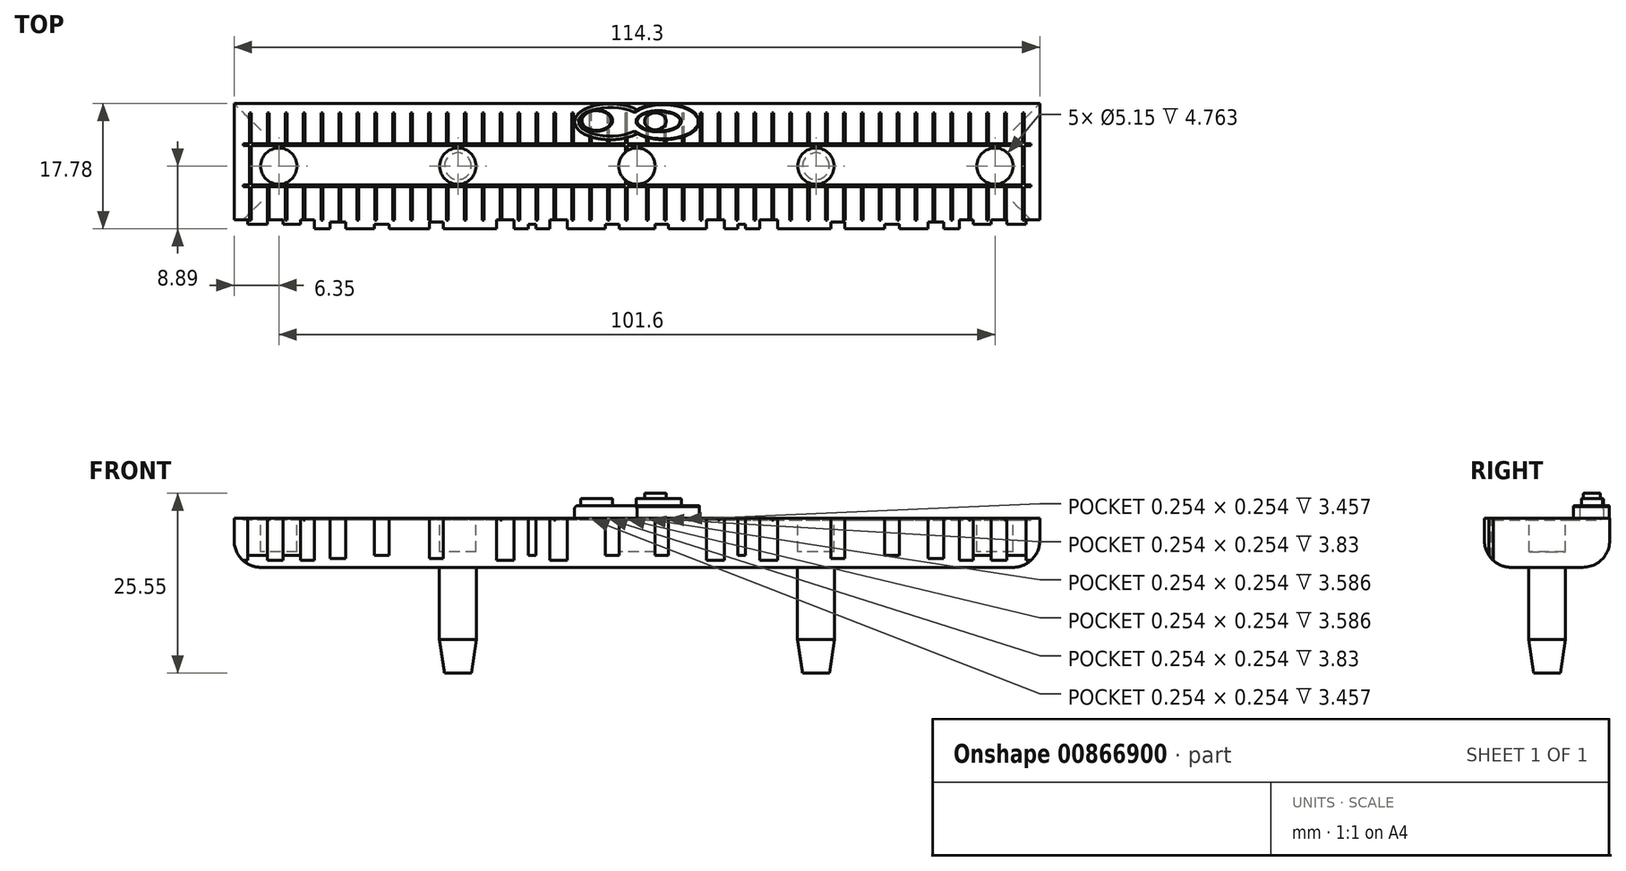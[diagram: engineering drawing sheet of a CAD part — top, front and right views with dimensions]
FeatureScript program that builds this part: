
annotation { "Feature Type Name" : "Feature", "Feature Type Description" : "" }
export const myFeature = defineFeature(function(context is Context, id is Id, definition is map)
    precondition{}
    {
        {
            var Q0;
            Q0=qCreatedBy(makeId("Top.planeOp"),FACE);
            var sketch = newSketch(context, id + "F0", { "sketchPlane" : qUnion([Q0])});
            skLineSegment(sketch, "E0.bottom", {"start": v(57.15, 8.9) * mm, "end": v(-57.15, 8.9) * mm});
            skLineSegment(sketch, "E0.top", {"start": v(57.15, -8.9) * mm, "end": v(-57.15, -8.9) * mm});
            skLineSegment(sketch, "E0.left", {"start": v(57.15, 8.9) * mm, "end": v(57.15, -8.9) * mm});
            skLineSegment(sketch, "E0.right", {"start": v(-57.15, 8.9) * mm, "end": v(-57.15, -8.9) * mm});
            skPoint(sketch, "E0.middle", {"position": v(0, 0) * mm});
            skSolve(sketch);
        }
        {
            var Q0;
            Q0=makeQuery(id+"F0.imprint","IMPRINT",FACE,{"disambiguationData":[TD([[makeQuery(id+"F0.imprint","IMPRINT",EDGE,{"derivedFrom":sQuery(id+"F0.wireOp",EDGE,"E0.bottom")}),1.0]])]});
            extrude(context, id + "F1", {"entities" : qUnion([Q0]), "oppositeDirection" : true, "depth" : 7 * mm, "offsetDistance" : 25.4 * mm});
        }
        {
            var Q0;
            Q0=qCreatedBy(makeId("Top.planeOp"),FACE);
            var sketch = newSketch(context, id + "F2", { "sketchPlane" : qUnion([Q0])});
            skLineSegment(sketch, "E1", {"start": v(0, 0) * mm, "end": v(25.4, 0) * mm, "construction": true});
            skLineSegment(sketch, "E2", {"start": v(25.4, 0) * mm, "end": v(50.8, 0) * mm, "construction": true});
            skLineSegment(sketch, "E3", {"start": v(0, 0) * mm, "end": v(-25.4, 0) * mm, "construction": true});
            skLineSegment(sketch, "E4", {"start": v(-25.4, 0) * mm, "end": v(-50.8, 0) * mm, "construction": true});
            skCircle(sketch, "E5", {"center": v(-50.8, 0) * mm, "radius": 2.58 * mm});
            skCircle(sketch, "E6", {"center": v(-25.4, 0) * mm, "radius": 2.58 * mm});
            skCircle(sketch, "E7", {"center": v(0, 0) * mm, "radius": 2.58 * mm});
            skCircle(sketch, "E8", {"center": v(25.4, 0) * mm, "radius": 2.58 * mm});
            skCircle(sketch, "E9", {"center": v(50.8, 0) * mm, "radius": 2.58 * mm});
            skSolve(sketch);
        }
        {
            var Q0;
            Q0=makeQuery(id+"F1.opExtrude","CAP_FACE",FACE,{"disambiguationData":[OSD([sQuery(id+"F0.wireOp",EDGE,"E0.bottom"),sQuery(id+"F0.wireOp",EDGE,"E0.top"),sQuery(id+"F0.wireOp",EDGE,"E0.left"),sQuery(id+"F0.wireOp",EDGE,"E0.right")])],"isStart":false});
            var sketch = newSketch(context, id + "F3", { "sketchPlane" : qUnion([Q0])});
            skLineSegment(sketch, "E10", {"start": v(0, 0) * mm, "end": v(25.4, 0) * mm, "construction": true});
            skLineSegment(sketch, "E11", {"start": v(25.4, 0) * mm, "end": v(50.8, 0) * mm, "construction": true});
            skLineSegment(sketch, "E12", {"start": v(0, 0) * mm, "end": v(-25.4, 0) * mm, "construction": true});
            skLineSegment(sketch, "E13", {"start": v(-25.4, 0) * mm, "end": v(-50.8, 0) * mm, "construction": true});
            skCircle(sketch, "E14", {"center": v(-50.8, 0) * mm, "radius": 2.62 * mm});
            skCircle(sketch, "E15", {"center": v(-25.4, 0) * mm, "radius": 2.62 * mm});
            skCircle(sketch, "E16", {"center": v(0, 0) * mm, "radius": 2.62 * mm});
            skCircle(sketch, "E17", {"center": v(25.4, 0) * mm, "radius": 2.62 * mm});
            skCircle(sketch, "E18", {"center": v(50.8, 0) * mm, "radius": 2.62 * mm});
            skSolve(sketch);
        }
        {
            var Q0;
            Q0=makeQuery(id+"F2.imprint","IMPRINT",FACE,{"disambiguationData":[TD([[makeQuery(id+"F2.imprint","IMPRINT",EDGE,{"derivedFrom":sQuery(id+"F2.wireOp",EDGE,"E5")}),1.0]])]});
            var Q1;
            Q1=makeQuery(id+"F2.imprint","IMPRINT",FACE,{"disambiguationData":[TD([[makeQuery(id+"F2.imprint","IMPRINT",EDGE,{"derivedFrom":sQuery(id+"F2.wireOp",EDGE,"E6")}),1.0]])]});
            var Q2;
            Q2=makeQuery(id+"F2.imprint","IMPRINT",FACE,{"disambiguationData":[TD([[makeQuery(id+"F2.imprint","IMPRINT",EDGE,{"derivedFrom":sQuery(id+"F2.wireOp",EDGE,"E7")}),1.0]])]});
            var Q3;
            Q3=makeQuery(id+"F2.imprint","IMPRINT",FACE,{"disambiguationData":[TD([[makeQuery(id+"F2.imprint","IMPRINT",EDGE,{"derivedFrom":sQuery(id+"F2.wireOp",EDGE,"E8")}),1.0]])]});
            var Q4;
            Q4=makeQuery(id+"F2.imprint","IMPRINT",FACE,{"disambiguationData":[TD([[makeQuery(id+"F2.imprint","IMPRINT",EDGE,{"derivedFrom":sQuery(id+"F2.wireOp",EDGE,"E9")}),1.0]])]});
            extrude(context, id + "F4", {"entities" : qUnion([Q0, Q1, Q2, Q3, Q4]), "operationType" : NewBodyOperationType.REMOVE, "oppositeDirection" : true, "depth" : 4.76 * mm, "offsetDistance" : 25.4 * mm});
        }
        {
            var Q0;
            Q0=makeQuery(id+"F3.imprint","IMPRINT",FACE,{"disambiguationData":[TD([[makeQuery(id+"F3.imprint","IMPRINT",EDGE,{"derivedFrom":sQuery(id+"F3.wireOp",EDGE,"E15")}),1.0]])]});
            var Q1;
            Q1=makeQuery(id+"F3.imprint","IMPRINT",FACE,{"disambiguationData":[TD([[makeQuery(id+"F3.imprint","IMPRINT",EDGE,{"derivedFrom":sQuery(id+"F3.wireOp",EDGE,"E17")}),1.0]])]});
            extrude(context, id + "F5", {"entities" : qUnion([Q0, Q1]), "operationType" : NewBodyOperationType.ADD, "depth" : 15 * mm, "offsetDistance" : 25.4 * mm});
        }
        {
            var Q0;
            Q0=makeQuery(id+"F5.opExtrude","CAP_EDGE",EDGE,{"disambiguationData":[OSD([sQuery(id+"F3.wireOp",EDGE,"E15")])],"isStart":false});
            var Q1;
            Q1=makeQuery(id+"F5.opExtrude","CAP_EDGE",EDGE,{"disambiguationData":[OSD([sQuery(id+"F3.wireOp",EDGE,"E17")])],"isStart":false});
            chamfer(context, id + "F6", {"entities" : qUnion([Q0, Q1]), "chamferType" : ChamferType.TWO_OFFSETS, "width1" : 0.73 * mm, "oppositeDirection" : false, "width2" : 4.76 * mm, "tangentPropagation" : true});
        }
        {
            var Q0;
            Q0=makeQuery(id+"F1.opExtrude","CAP_EDGE",EDGE,{"disambiguationData":[OSD([sQuery(id+"F0.wireOp",EDGE,"E0.top")])],"isStart":false});
            var Q1;
            Q1=makeQuery(id+"F1.opExtrude","CAP_EDGE",EDGE,{"disambiguationData":[OSD([sQuery(id+"F0.wireOp",EDGE,"E0.left")])],"isStart":false});
            var Q2;
            Q2=makeQuery(id+"F1.opExtrude","CAP_EDGE",EDGE,{"disambiguationData":[OSD([sQuery(id+"F0.wireOp",EDGE,"E0.bottom")])],"isStart":false});
            var Q3;
            Q3=makeQuery(id+"F1.opExtrude","CAP_EDGE",EDGE,{"disambiguationData":[OSD([sQuery(id+"F0.wireOp",EDGE,"E0.right")])],"isStart":false});
            fillet(context, id + "F7", {"entities" : qUnion([Q0, Q1, Q2, Q3]), "radius" : 3.8 * mm, "tangentPropagation" : true, "allowEdgeOverflow" : false});
        }
        {
            var Q0;
            Q0=makeQuery(id+"F1.opExtrude","CAP_FACE",FACE,{"disambiguationData":[OSD([sQuery(id+"F0.wireOp",EDGE,"E0.bottom"),sQuery(id+"F0.wireOp",EDGE,"E0.top"),sQuery(id+"F0.wireOp",EDGE,"E0.left"),sQuery(id+"F0.wireOp",EDGE,"E0.right")])],"isStart":true});
            var sketch = newSketch(context, id + "F8", { "sketchPlane" : qUnion([Q0])});
            skLineSegment(sketch, "E19.bottom", {"start": v(57.15, -8.9) * mm, "end": v(55.22, -8.9) * mm});
            skLineSegment(sketch, "E19.top", {"start": v(57.15, -7.63) * mm, "end": v(55.22, -7.63) * mm});
            skLineSegment(sketch, "E19.left", {"start": v(57.15, -8.9) * mm, "end": v(57.15, -7.63) * mm});
            skLineSegment(sketch, "E19.right", {"start": v(55.22, -8.26) * mm, "end": v(55.22, -7.63) * mm});
            skPoint(sketch, "E20.oppositeSnap0", {"position": v(55.22, -8.26) * mm});
            skLineSegment(sketch, "E20.bottom", {"start": v(55.22, -8.9) * mm, "end": v(52.44, -8.9) * mm});
            skLineSegment(sketch, "E20.top", {"start": v(55.22, -8.26) * mm, "end": v(52.44, -8.26) * mm});
            skLineSegment(sketch, "E21.bottom", {"start": v(52.44, -8.9) * mm, "end": v(50.22, -8.9) * mm});
            skLineSegment(sketch, "E21.top", {"start": v(52.44, -7.63) * mm, "end": v(50.22, -7.63) * mm});
            skLineSegment(sketch, "E21.left", {"start": v(52.44, -8.26) * mm, "end": v(52.44, -7.63) * mm});
            skLineSegment(sketch, "E21.right", {"start": v(50.22, -8.26) * mm, "end": v(50.22, -7.63) * mm});
            skLineSegment(sketch, "E22.bottom", {"start": v(50.22, -8.9) * mm, "end": v(47.71, -8.9) * mm});
            skLineSegment(sketch, "E22.top", {"start": v(50.22, -8.26) * mm, "end": v(47.71, -8.26) * mm});
            skLineSegment(sketch, "E23.bottom", {"start": v(47.71, -8.9) * mm, "end": v(45.77, -8.9) * mm});
            skLineSegment(sketch, "E23.top", {"start": v(47.71, -7.63) * mm, "end": v(45.77, -7.63) * mm});
            skLineSegment(sketch, "E23.left", {"start": v(47.71, -8.26) * mm, "end": v(47.71, -7.63) * mm});
            skLineSegment(sketch, "E23.right", {"start": v(45.77, -8.9) * mm, "end": v(45.77, -7.63) * mm});
            skLineSegment(sketch, "E24.bottom", {"start": v(43.54, -8.9) * mm, "end": v(41.32, -8.9) * mm});
            skLineSegment(sketch, "E24.top", {"start": v(43.54, -7.91) * mm, "end": v(41.32, -7.91) * mm});
            skLineSegment(sketch, "E24.left", {"start": v(43.54, -8.9) * mm, "end": v(43.54, -7.91) * mm});
            skLineSegment(sketch, "E24.right", {"start": v(41.32, -8.9) * mm, "end": v(41.32, -7.91) * mm});
            skLineSegment(sketch, "E25.bottom", {"start": v(35.14, -8.9) * mm, "end": v(37.24, -8.9) * mm});
            skLineSegment(sketch, "E25.top", {"start": v(35.14, -8.26) * mm, "end": v(37.24, -8.26) * mm});
            skLineSegment(sketch, "E25.left", {"start": v(35.14, -8.9) * mm, "end": v(35.14, -8.26) * mm});
            skLineSegment(sketch, "E25.right", {"start": v(37.24, -8.9) * mm, "end": v(37.24, -8.26) * mm});
            skLineSegment(sketch, "E26.bottom", {"start": v(29.46, -8.9) * mm, "end": v(27.49, -8.9) * mm});
            skLineSegment(sketch, "E26.top", {"start": v(29.46, -7.91) * mm, "end": v(27.49, -7.91) * mm});
            skLineSegment(sketch, "E26.left", {"start": v(29.46, -8.9) * mm, "end": v(29.46, -7.91) * mm});
            skLineSegment(sketch, "E26.right", {"start": v(27.49, -8.9) * mm, "end": v(27.49, -7.91) * mm});
            skLineSegment(sketch, "E27.bottom", {"start": v(19.95, -8.9) * mm, "end": v(17.43, -8.9) * mm});
            skLineSegment(sketch, "E27.top", {"start": v(19.95, -7.63) * mm, "end": v(17.43, -7.63) * mm});
            skLineSegment(sketch, "E27.left", {"start": v(19.95, -8.9) * mm, "end": v(19.95, -7.63) * mm});
            skLineSegment(sketch, "E27.right", {"start": v(17.43, -8.9) * mm, "end": v(17.43, -7.63) * mm});
            skPoint(sketch, "E28.oppositeSnap0", {"position": v(18.69, -7.63) * mm});
            skLineSegment(sketch, "E28.bottom", {"start": v(12.38, -8.9) * mm, "end": v(9.86, -8.9) * mm});
            skLineSegment(sketch, "E28.top", {"start": v(12.38, -7.63) * mm, "end": v(9.86, -7.63) * mm});
            skLineSegment(sketch, "E28.left", {"start": v(12.38, -8.9) * mm, "end": v(12.38, -7.63) * mm});
            skLineSegment(sketch, "E28.right", {"start": v(9.86, -8.9) * mm, "end": v(9.86, -7.63) * mm});
            skLineSegment(sketch, "E29.bottom", {"start": v(14.33, -8.9) * mm, "end": v(15.42, -8.9) * mm});
            skLineSegment(sketch, "E29.top", {"start": v(14.33, -8.26) * mm, "end": v(15.42, -8.26) * mm});
            skLineSegment(sketch, "E29.left", {"start": v(14.33, -8.9) * mm, "end": v(14.33, -8.26) * mm});
            skLineSegment(sketch, "E29.right", {"start": v(15.42, -8.9) * mm, "end": v(15.42, -8.26) * mm});
            skLineSegment(sketch, "E30.bottom", {"start": v(2.53, -8.9) * mm, "end": v(4.48, -8.9) * mm});
            skLineSegment(sketch, "E30.top", {"start": v(2.53, -8.26) * mm, "end": v(4.48, -8.26) * mm});
            skLineSegment(sketch, "E30.left", {"start": v(2.53, -8.9) * mm, "end": v(2.53, -8.26) * mm});
            skLineSegment(sketch, "E30.right", {"start": v(4.48, -8.9) * mm, "end": v(4.48, -8.26) * mm});
            skLineSegment(sketch, "E31", {"start": v(0, 15.07) * mm, "end": v(0, 19.04) * mm, "construction": true});
            skLineSegment(sketch, "E32.MirrorCS", {"start": v(-50.22, -8.26) * mm, "end": v(-50.22, -7.63) * mm});
            skLineSegment(sketch, "E33.MirrorCS", {"start": v(-52.44, -8.26) * mm, "end": v(-52.44, -7.63) * mm});
            skLineSegment(sketch, "E34.MirrorCS", {"start": v(-52.44, -7.63) * mm, "end": v(-50.22, -7.63) * mm});
            skLineSegment(sketch, "E35.MirrorCS", {"start": v(-52.44, -8.9) * mm, "end": v(-50.22, -8.9) * mm});
            skLineSegment(sketch, "E36.MirrorCS", {"start": v(-57.15, -7.63) * mm, "end": v(-55.22, -7.63) * mm});
            skLineSegment(sketch, "E37.MirrorCS", {"start": v(-55.22, -8.26) * mm, "end": v(-52.44, -8.26) * mm});
            skLineSegment(sketch, "E38.MirrorCS", {"start": v(-14.33, -8.9) * mm, "end": v(-14.33, -8.26) * mm});
            skLineSegment(sketch, "E39.MirrorCS", {"start": v(-55.22, -8.9) * mm, "end": v(-52.44, -8.9) * mm});
            skLineSegment(sketch, "E40.MirrorCS", {"start": v(-15.42, -8.9) * mm, "end": v(-15.42, -8.26) * mm});
            skLineSegment(sketch, "E41.MirrorCS", {"start": v(-57.15, -8.9) * mm, "end": v(-55.22, -8.9) * mm});
            skLineSegment(sketch, "E42.MirrorCS", {"start": v(-50.22, -8.26) * mm, "end": v(-47.71, -8.26) * mm});
            skLineSegment(sketch, "E43.MirrorCS", {"start": v(-55.22, -8.26) * mm, "end": v(-55.22, -7.63) * mm});
            skLineSegment(sketch, "E44.MirrorCS", {"start": v(-50.22, -8.9) * mm, "end": v(-47.71, -8.9) * mm});
            skLineSegment(sketch, "E45.MirrorCS", {"start": v(-14.33, -8.26) * mm, "end": v(-15.42, -8.26) * mm});
            skLineSegment(sketch, "E46.MirrorCS", {"start": v(-2.53, -8.9) * mm, "end": v(-2.53, -8.26) * mm});
            skLineSegment(sketch, "E47.MirrorCS", {"start": v(-47.71, -7.63) * mm, "end": v(-45.77, -7.63) * mm});
            skLineSegment(sketch, "E48.MirrorCS", {"start": v(-35.14, -8.9) * mm, "end": v(-35.14, -8.26) * mm});
            skLineSegment(sketch, "E49.MirrorCS", {"start": v(-47.71, -8.26) * mm, "end": v(-47.71, -7.63) * mm});
            skLineSegment(sketch, "E50.MirrorCS", {"start": v(-37.24, -8.9) * mm, "end": v(-37.24, -8.26) * mm});
            skLineSegment(sketch, "E51.MirrorCS", {"start": v(-12.38, -8.9) * mm, "end": v(-12.38, -7.63) * mm});
            skLineSegment(sketch, "E52.MirrorCS", {"start": v(-17.43, -8.9) * mm, "end": v(-17.43, -7.63) * mm});
            skLineSegment(sketch, "E53.MirrorCS", {"start": v(-47.71, -8.9) * mm, "end": v(-45.77, -8.9) * mm});
            skLineSegment(sketch, "E54.MirrorCS", {"start": v(-14.33, -8.9) * mm, "end": v(-15.42, -8.9) * mm});
            skLineSegment(sketch, "E55.MirrorCS", {"start": v(-4.48, -8.9) * mm, "end": v(-4.48, -8.26) * mm});
            skLineSegment(sketch, "E56.MirrorCS", {"start": v(-35.14, -8.9) * mm, "end": v(-37.24, -8.9) * mm});
            skLineSegment(sketch, "E57.MirrorCS", {"start": v(-2.53, -8.9) * mm, "end": v(-4.48, -8.9) * mm});
            skLineSegment(sketch, "E58.MirrorCS", {"start": v(-2.53, -8.26) * mm, "end": v(-4.48, -8.26) * mm});
            skLineSegment(sketch, "E59.MirrorCS", {"start": v(-35.14, -8.26) * mm, "end": v(-37.24, -8.26) * mm});
            skLineSegment(sketch, "E60.MirrorCS", {"start": v(-19.95, -8.9) * mm, "end": v(-17.43, -8.9) * mm});
            skLineSegment(sketch, "E61.MirrorCS", {"start": v(-19.95, -7.63) * mm, "end": v(-17.43, -7.63) * mm});
            skLineSegment(sketch, "E62.MirrorCS", {"start": v(-12.38, -7.63) * mm, "end": v(-9.86, -7.63) * mm});
            skLineSegment(sketch, "E63.MirrorCS", {"start": v(-41.32, -8.9) * mm, "end": v(-41.32, -7.91) * mm});
            skLineSegment(sketch, "E64.MirrorCS", {"start": v(-45.77, -8.9) * mm, "end": v(-45.77, -7.63) * mm});
            skLineSegment(sketch, "E65.MirrorCS", {"start": v(-43.54, -8.9) * mm, "end": v(-43.54, -7.91) * mm});
            skLineSegment(sketch, "E66.MirrorCS", {"start": v(-43.54, -8.9) * mm, "end": v(-41.32, -8.9) * mm});
            skLineSegment(sketch, "E67.MirrorCS", {"start": v(-19.95, -8.9) * mm, "end": v(-19.95, -7.63) * mm});
            skLineSegment(sketch, "E68.MirrorCS", {"start": v(-43.54, -7.91) * mm, "end": v(-41.32, -7.91) * mm});
            skLineSegment(sketch, "E69.MirrorCS", {"start": v(-29.46, -8.9) * mm, "end": v(-29.46, -7.91) * mm});
            skLineSegment(sketch, "E70.MirrorCS", {"start": v(-29.46, -7.91) * mm, "end": v(-27.49, -7.91) * mm});
            skLineSegment(sketch, "E71.MirrorCS", {"start": v(-29.46, -8.9) * mm, "end": v(-27.49, -8.9) * mm});
            skLineSegment(sketch, "E72.MirrorCS", {"start": v(-27.49, -8.9) * mm, "end": v(-27.49, -7.91) * mm});
            skLineSegment(sketch, "E73.MirrorCS", {"start": v(-9.86, -8.9) * mm, "end": v(-9.86, -7.63) * mm});
            skLineSegment(sketch, "E74.MirrorCS", {"start": v(-57.15, -8.9) * mm, "end": v(-57.15, -7.63) * mm});
            skLineSegment(sketch, "E75.MirrorCS", {"start": v(-12.38, -8.9) * mm, "end": v(-9.86, -8.9) * mm});
            skPoint(sketch, "E76.MirrorP", {"position": v(-55.22, -8.26) * mm});
            skPoint(sketch, "E77.MirrorP", {"position": v(-18.69, -7.63) * mm});
            skSolve(sketch);
        }
        {
            var Q0;
            Q0=makeQuery(id+"F8.imprint","IMPRINT",FACE,{"disambiguationData":[TD([[makeQuery(id+"F8.imprint","IMPRINT",EDGE,{"derivedFrom":sQuery(id+"F8.wireOp",EDGE,"E30.bottom")}),-1.0]])]});
            var Q1;
            Q1=makeQuery(id+"F8.imprint","IMPRINT",FACE,{"disambiguationData":[TD([[makeQuery(id+"F8.imprint","IMPRINT",EDGE,{"derivedFrom":sQuery(id+"F8.wireOp",EDGE,"E28.bottom")}),-1.0]])]});
            var Q2;
            Q2=makeQuery(id+"F8.imprint","IMPRINT",FACE,{"disambiguationData":[TD([[makeQuery(id+"F8.imprint","IMPRINT",EDGE,{"derivedFrom":sQuery(id+"F8.wireOp",EDGE,"E29.bottom")}),-1.0]])]});
            var Q3;
            Q3=makeQuery(id+"F8.imprint","IMPRINT",FACE,{"disambiguationData":[TD([[makeQuery(id+"F8.imprint","IMPRINT",EDGE,{"derivedFrom":sQuery(id+"F8.wireOp",EDGE,"E27.bottom")}),-1.0]])]});
            var Q4;
            Q4=makeQuery(id+"F8.imprint","IMPRINT",FACE,{"disambiguationData":[TD([[makeQuery(id+"F8.imprint","IMPRINT",EDGE,{"derivedFrom":sQuery(id+"F8.wireOp",EDGE,"E26.bottom")}),-1.0]])]});
            var Q5;
            Q5=makeQuery(id+"F8.imprint","IMPRINT",FACE,{"disambiguationData":[TD([[makeQuery(id+"F8.imprint","IMPRINT",EDGE,{"derivedFrom":sQuery(id+"F8.wireOp",EDGE,"E25.bottom")}),-1.0]])]});
            var Q6;
            Q6=makeQuery(id+"F8.imprint","IMPRINT",FACE,{"disambiguationData":[TD([[makeQuery(id+"F8.imprint","IMPRINT",EDGE,{"derivedFrom":sQuery(id+"F8.wireOp",EDGE,"E24.bottom")}),-1.0]])]});
            var Q7;
            Q7=makeQuery(id+"F8.imprint","IMPRINT",FACE,{"disambiguationData":[TD([[makeQuery(id+"F8.imprint","IMPRINT",EDGE,{"derivedFrom":sQuery(id+"F8.wireOp",EDGE,"E19.bottom")}),-1.0]])]});
            var Q8;
            Q8=makeQuery(id+"F8.imprint","IMPRINT",FACE,{"disambiguationData":[TD([[makeQuery(id+"F8.imprint","IMPRINT",EDGE,{"derivedFrom":sQuery(id+"F8.wireOp",EDGE,"E46.MirrorCS")}),1.0]])]});
            var Q9;
            Q9=makeQuery(id+"F8.imprint","IMPRINT",FACE,{"disambiguationData":[TD([[makeQuery(id+"F8.imprint","IMPRINT",EDGE,{"derivedFrom":sQuery(id+"F8.wireOp",EDGE,"E51.MirrorCS")}),-1.0]])]});
            var Q10;
            Q10=makeQuery(id+"F8.imprint","IMPRINT",FACE,{"disambiguationData":[TD([[makeQuery(id+"F8.imprint","IMPRINT",EDGE,{"derivedFrom":sQuery(id+"F8.wireOp",EDGE,"E38.MirrorCS")}),1.0]])]});
            var Q11;
            Q11=makeQuery(id+"F8.imprint","IMPRINT",FACE,{"disambiguationData":[TD([[makeQuery(id+"F8.imprint","IMPRINT",EDGE,{"derivedFrom":sQuery(id+"F8.wireOp",EDGE,"E52.MirrorCS")}),1.0]])]});
            var Q12;
            Q12=makeQuery(id+"F8.imprint","IMPRINT",FACE,{"disambiguationData":[TD([[makeQuery(id+"F8.imprint","IMPRINT",EDGE,{"derivedFrom":sQuery(id+"F8.wireOp",EDGE,"E69.MirrorCS")}),-1.0]])]});
            var Q13;
            Q13=makeQuery(id+"F8.imprint","IMPRINT",FACE,{"disambiguationData":[TD([[makeQuery(id+"F8.imprint","IMPRINT",EDGE,{"derivedFrom":sQuery(id+"F8.wireOp",EDGE,"E48.MirrorCS")}),1.0]])]});
            var Q14;
            Q14=makeQuery(id+"F8.imprint","IMPRINT",FACE,{"disambiguationData":[TD([[makeQuery(id+"F8.imprint","IMPRINT",EDGE,{"derivedFrom":sQuery(id+"F8.wireOp",EDGE,"E63.MirrorCS")}),1.0]])]});
            var Q15;
            Q15=makeQuery(id+"F8.imprint","IMPRINT",FACE,{"disambiguationData":[TD([[makeQuery(id+"F8.imprint","IMPRINT",EDGE,{"derivedFrom":sQuery(id+"F8.wireOp",EDGE,"E32.MirrorCS")}),1.0]])]});
            extrude(context, id + "F9", {"entities" : qUnion([Q0, Q1, Q2, Q3, Q4, Q5, Q6, Q7, Q8, Q9, Q10, Q11, Q12, Q13, Q14, Q15]), "operationType" : NewBodyOperationType.REMOVE, "endBound" : BoundingType.THROUGH_ALL, "oppositeDirection" : true, "depth" : 25.4 * mm, "offsetDistance" : 25.4 * mm});
        }
        {
            var Q0;
            Q0=makeQuery(id+"F1.opExtrude","CAP_FACE",FACE,{"disambiguationData":[OSD([sQuery(id+"F0.wireOp",EDGE,"E0.bottom"),sQuery(id+"F0.wireOp",EDGE,"E0.top"),sQuery(id+"F0.wireOp",EDGE,"E0.left"),sQuery(id+"F0.wireOp",EDGE,"E0.right")])],"isStart":true});
            var sketch = newSketch(context, id + "F10", { "sketchPlane" : qUnion([Q0])});
            skLineSegment(sketch, "E78", {"start": v(0, 4.02) * mm, "end": v(0, 5.57) * mm, "construction": true});
            skLineSegment(sketch, "E79", {"start": v(0, 2.94) * mm, "end": v(55.88, 2.94) * mm});
            skLineSegment(sketch, "E80", {"start": v(0, -2.68) * mm, "end": v(55.88, -2.68) * mm});
            skLineSegment(sketch, "E81.top", {"start": v(0, 3.2) * mm, "end": v(55.88, 3.2) * mm});
            skLineSegment(sketch, "E81.left", {"start": v(0, 2.94) * mm, "end": v(0, 3.2) * mm});
            skLineSegment(sketch, "E81.right", {"start": v(55.88, 2.94) * mm, "end": v(55.88, 3.2) * mm});
            skLineSegment(sketch, "E82.top", {"start": v(0, -2.93) * mm, "end": v(55.88, -2.93) * mm});
            skLineSegment(sketch, "E82.left", {"start": v(0, -2.68) * mm, "end": v(0, -2.93) * mm});
            skLineSegment(sketch, "E82.right", {"start": v(55.88, -2.68) * mm, "end": v(55.88, -2.93) * mm});
            skLineSegment(sketch, "E83.bottom", {"start": v(1.36, -7.65) * mm, "end": v(1.61, -7.65) * mm});
            skLineSegment(sketch, "E83.top", {"start": v(1.36, 7.59) * mm, "end": v(1.61, 7.59) * mm});
            skLineSegment(sketch, "E83.left", {"start": v(1.36, -7.65) * mm, "end": v(1.36, 7.59) * mm});
            skLineSegment(sketch, "E83.right", {"start": v(1.61, -7.65) * mm, "end": v(1.61, 7.59) * mm});
            skLineSegment(sketch, "E84.MirrorCS", {"start": v(-55.88, -2.68) * mm, "end": v(-55.88, -2.93) * mm});
            skLineSegment(sketch, "E85.MirrorCS", {"start": v(-55.88, 2.94) * mm, "end": v(-55.88, 3.2) * mm});
            skLineSegment(sketch, "E86.MirrorCS", {"start": v(-1.36, -7.65) * mm, "end": v(-1.61, -7.65) * mm});
            skLineSegment(sketch, "E87.MirrorCS", {"start": v(0, -2.68) * mm, "end": v(-55.88, -2.68) * mm});
            skLineSegment(sketch, "E88.MirrorCS", {"start": v(-1.36, 7.59) * mm, "end": v(-1.61, 7.59) * mm});
            skLineSegment(sketch, "E89.MirrorCS", {"start": v(0, 2.94) * mm, "end": v(-55.88, 2.94) * mm});
            skLineSegment(sketch, "E90.MirrorCS", {"start": v(0, -2.93) * mm, "end": v(-55.88, -2.93) * mm});
            skLineSegment(sketch, "E91.MirrorCS", {"start": v(-1.61, -7.65) * mm, "end": v(-1.61, 7.59) * mm});
            skLineSegment(sketch, "E92.MirrorCS", {"start": v(-1.36, -7.65) * mm, "end": v(-1.36, 7.59) * mm});
            skLineSegment(sketch, "E93.MirrorCS", {"start": v(0, 3.2) * mm, "end": v(-55.88, 3.2) * mm});
            skLineSegment(sketch, "E94.1.0.0", {"start": v(3.9, -7.65) * mm, "end": v(3.9, 7.59) * mm});
            skLineSegment(sketch, "E94.1.0.1", {"start": v(4.15, -7.65) * mm, "end": v(4.15, 7.59) * mm});
            skLineSegment(sketch, "E94.1.0.2", {"start": v(3.9, 7.59) * mm, "end": v(4.15, 7.59) * mm});
            skLineSegment(sketch, "E94.1.0.3", {"start": v(3.9, -7.65) * mm, "end": v(4.15, -7.65) * mm});
            skLineSegment(sketch, "E94.2.0.0", {"start": v(6.44, -7.65) * mm, "end": v(6.44, 7.59) * mm});
            skLineSegment(sketch, "E94.2.0.1", {"start": v(6.7, -7.65) * mm, "end": v(6.7, 7.59) * mm});
            skLineSegment(sketch, "E94.2.0.2", {"start": v(6.44, 7.59) * mm, "end": v(6.7, 7.59) * mm});
            skLineSegment(sketch, "E94.2.0.3", {"start": v(6.44, -7.65) * mm, "end": v(6.7, -7.65) * mm});
            skLineSegment(sketch, "E94.3.0.0", {"start": v(8.98, -7.65) * mm, "end": v(8.98, 7.59) * mm});
            skLineSegment(sketch, "E94.3.0.1", {"start": v(9.23, -7.65) * mm, "end": v(9.23, 7.59) * mm});
            skLineSegment(sketch, "E94.3.0.2", {"start": v(8.98, 7.59) * mm, "end": v(9.23, 7.59) * mm});
            skLineSegment(sketch, "E94.3.0.3", {"start": v(8.98, -7.65) * mm, "end": v(9.23, -7.65) * mm});
            skLineSegment(sketch, "E94.4.0.0", {"start": v(11.52, -7.65) * mm, "end": v(11.52, 7.59) * mm});
            skLineSegment(sketch, "E94.4.0.1", {"start": v(11.77, -7.65) * mm, "end": v(11.77, 7.59) * mm});
            skLineSegment(sketch, "E94.4.0.2", {"start": v(11.52, 7.59) * mm, "end": v(11.77, 7.59) * mm});
            skLineSegment(sketch, "E94.4.0.3", {"start": v(11.52, -7.65) * mm, "end": v(11.77, -7.65) * mm});
            skLineSegment(sketch, "E94.5.0.0", {"start": v(14.06, -7.65) * mm, "end": v(14.06, 7.59) * mm});
            skLineSegment(sketch, "E94.5.0.1", {"start": v(14.31, -7.65) * mm, "end": v(14.31, 7.59) * mm});
            skLineSegment(sketch, "E94.5.0.2", {"start": v(14.06, 7.59) * mm, "end": v(14.31, 7.59) * mm});
            skLineSegment(sketch, "E94.5.0.3", {"start": v(14.06, -7.65) * mm, "end": v(14.31, -7.65) * mm});
            skLineSegment(sketch, "E94.6.0.0", {"start": v(16.6, -7.65) * mm, "end": v(16.6, 7.59) * mm});
            skLineSegment(sketch, "E94.6.0.1", {"start": v(16.85, -7.65) * mm, "end": v(16.85, 7.59) * mm});
            skLineSegment(sketch, "E94.6.0.2", {"start": v(16.6, 7.59) * mm, "end": v(16.85, 7.59) * mm});
            skLineSegment(sketch, "E94.6.0.3", {"start": v(16.6, -7.65) * mm, "end": v(16.85, -7.65) * mm});
            skLineSegment(sketch, "E94.7.0.0", {"start": v(19.14, -7.65) * mm, "end": v(19.14, 7.59) * mm});
            skLineSegment(sketch, "E94.7.0.1", {"start": v(19.4, -7.65) * mm, "end": v(19.4, 7.59) * mm});
            skLineSegment(sketch, "E94.7.0.2", {"start": v(19.14, 7.59) * mm, "end": v(19.4, 7.59) * mm});
            skLineSegment(sketch, "E94.7.0.3", {"start": v(19.14, -7.65) * mm, "end": v(19.4, -7.65) * mm});
            skLineSegment(sketch, "E94.8.0.0", {"start": v(21.68, -7.65) * mm, "end": v(21.68, 7.59) * mm});
            skLineSegment(sketch, "E94.8.0.1", {"start": v(21.93, -7.65) * mm, "end": v(21.93, 7.59) * mm});
            skLineSegment(sketch, "E94.8.0.2", {"start": v(21.68, 7.59) * mm, "end": v(21.93, 7.59) * mm});
            skLineSegment(sketch, "E94.8.0.3", {"start": v(21.68, -7.65) * mm, "end": v(21.93, -7.65) * mm});
            skLineSegment(sketch, "E94.9.0.0", {"start": v(24.22, -7.65) * mm, "end": v(24.22, 7.59) * mm});
            skLineSegment(sketch, "E94.9.0.1", {"start": v(24.47, -7.65) * mm, "end": v(24.47, 7.59) * mm});
            skLineSegment(sketch, "E94.9.0.2", {"start": v(24.22, 7.59) * mm, "end": v(24.47, 7.59) * mm});
            skLineSegment(sketch, "E94.9.0.3", {"start": v(24.22, -7.65) * mm, "end": v(24.47, -7.65) * mm});
            skLineSegment(sketch, "E94.10.0.0", {"start": v(26.76, -7.65) * mm, "end": v(26.76, 7.59) * mm});
            skLineSegment(sketch, "E94.10.0.1", {"start": v(27.01, -7.65) * mm, "end": v(27.01, 7.59) * mm});
            skLineSegment(sketch, "E94.10.0.2", {"start": v(26.76, 7.59) * mm, "end": v(27.01, 7.59) * mm});
            skLineSegment(sketch, "E94.10.0.3", {"start": v(26.76, -7.65) * mm, "end": v(27.01, -7.65) * mm});
            skLineSegment(sketch, "E94.11.0.0", {"start": v(29.3, -7.65) * mm, "end": v(29.3, 7.59) * mm});
            skLineSegment(sketch, "E94.11.0.1", {"start": v(29.55, -7.65) * mm, "end": v(29.55, 7.59) * mm});
            skLineSegment(sketch, "E94.11.0.2", {"start": v(29.3, 7.59) * mm, "end": v(29.55, 7.59) * mm});
            skLineSegment(sketch, "E94.11.0.3", {"start": v(29.3, -7.65) * mm, "end": v(29.55, -7.65) * mm});
            skLineSegment(sketch, "E94.12.0.0", {"start": v(31.84, -7.65) * mm, "end": v(31.84, 7.59) * mm});
            skLineSegment(sketch, "E94.12.0.1", {"start": v(32.1, -7.65) * mm, "end": v(32.1, 7.59) * mm});
            skLineSegment(sketch, "E94.12.0.2", {"start": v(31.84, 7.59) * mm, "end": v(32.1, 7.59) * mm});
            skLineSegment(sketch, "E94.12.0.3", {"start": v(31.84, -7.65) * mm, "end": v(32.1, -7.65) * mm});
            skLineSegment(sketch, "E94.13.0.0", {"start": v(34.38, -7.65) * mm, "end": v(34.38, 7.59) * mm});
            skLineSegment(sketch, "E94.13.0.1", {"start": v(34.63, -7.65) * mm, "end": v(34.63, 7.59) * mm});
            skLineSegment(sketch, "E94.13.0.2", {"start": v(34.38, 7.59) * mm, "end": v(34.63, 7.59) * mm});
            skLineSegment(sketch, "E94.13.0.3", {"start": v(34.38, -7.65) * mm, "end": v(34.63, -7.65) * mm});
            skLineSegment(sketch, "E94.14.0.0", {"start": v(36.92, -7.65) * mm, "end": v(36.92, 7.59) * mm});
            skLineSegment(sketch, "E94.14.0.1", {"start": v(37.17, -7.65) * mm, "end": v(37.17, 7.59) * mm});
            skLineSegment(sketch, "E94.14.0.2", {"start": v(36.92, 7.59) * mm, "end": v(37.17, 7.59) * mm});
            skLineSegment(sketch, "E94.14.0.3", {"start": v(36.92, -7.65) * mm, "end": v(37.17, -7.65) * mm});
            skLineSegment(sketch, "E94.15.0.0", {"start": v(39.46, -7.65) * mm, "end": v(39.46, 7.59) * mm});
            skLineSegment(sketch, "E94.15.0.1", {"start": v(39.71, -7.65) * mm, "end": v(39.71, 7.59) * mm});
            skLineSegment(sketch, "E94.15.0.2", {"start": v(39.46, 7.59) * mm, "end": v(39.71, 7.59) * mm});
            skLineSegment(sketch, "E94.15.0.3", {"start": v(39.46, -7.65) * mm, "end": v(39.71, -7.65) * mm});
            skLineSegment(sketch, "E94.16.0.0", {"start": v(42, -7.65) * mm, "end": v(42, 7.59) * mm});
            skLineSegment(sketch, "E94.16.0.1", {"start": v(42.25, -7.65) * mm, "end": v(42.25, 7.59) * mm});
            skLineSegment(sketch, "E94.16.0.2", {"start": v(42, 7.59) * mm, "end": v(42.25, 7.59) * mm});
            skLineSegment(sketch, "E94.16.0.3", {"start": v(42, -7.65) * mm, "end": v(42.25, -7.65) * mm});
            skLineSegment(sketch, "E94.17.0.0", {"start": v(44.54, -7.65) * mm, "end": v(44.54, 7.59) * mm});
            skLineSegment(sketch, "E94.17.0.1", {"start": v(44.8, -7.65) * mm, "end": v(44.8, 7.59) * mm});
            skLineSegment(sketch, "E94.17.0.2", {"start": v(44.54, 7.59) * mm, "end": v(44.8, 7.59) * mm});
            skLineSegment(sketch, "E94.17.0.3", {"start": v(44.54, -7.65) * mm, "end": v(44.8, -7.65) * mm});
            skLineSegment(sketch, "E94.18.0.0", {"start": v(47.08, -7.65) * mm, "end": v(47.08, 7.59) * mm});
            skLineSegment(sketch, "E94.18.0.1", {"start": v(47.33, -7.65) * mm, "end": v(47.33, 7.59) * mm});
            skLineSegment(sketch, "E94.18.0.2", {"start": v(47.08, 7.59) * mm, "end": v(47.33, 7.59) * mm});
            skLineSegment(sketch, "E94.18.0.3", {"start": v(47.08, -7.65) * mm, "end": v(47.33, -7.65) * mm});
            skLineSegment(sketch, "E94.19.0.0", {"start": v(49.62, -7.65) * mm, "end": v(49.62, 7.59) * mm});
            skLineSegment(sketch, "E94.19.0.1", {"start": v(49.87, -7.65) * mm, "end": v(49.87, 7.59) * mm});
            skLineSegment(sketch, "E94.19.0.2", {"start": v(49.62, 7.59) * mm, "end": v(49.87, 7.59) * mm});
            skLineSegment(sketch, "E94.19.0.3", {"start": v(49.62, -7.65) * mm, "end": v(49.87, -7.65) * mm});
            skLineSegment(sketch, "E94.20.0.0", {"start": v(52.16, -7.65) * mm, "end": v(52.16, 7.59) * mm});
            skLineSegment(sketch, "E94.20.0.1", {"start": v(52.41, -7.65) * mm, "end": v(52.41, 7.59) * mm});
            skLineSegment(sketch, "E94.20.0.2", {"start": v(52.16, 7.59) * mm, "end": v(52.41, 7.59) * mm});
            skLineSegment(sketch, "E94.20.0.3", {"start": v(52.16, -7.65) * mm, "end": v(52.41, -7.65) * mm});
            skLineSegment(sketch, "E94.21.0.0", {"start": v(54.7, -7.65) * mm, "end": v(54.7, 7.59) * mm});
            skLineSegment(sketch, "E94.21.0.1", {"start": v(54.95, -7.65) * mm, "end": v(54.95, 7.59) * mm});
            skLineSegment(sketch, "E94.21.0.2", {"start": v(54.7, 7.59) * mm, "end": v(54.95, 7.59) * mm});
            skLineSegment(sketch, "E94.21.0.3", {"start": v(54.7, -7.65) * mm, "end": v(54.95, -7.65) * mm});
            skLineSegment(sketch, "E94.direction1", {"start": v(1.36, -7.65) * mm, "end": v(3.9, -7.65) * mm, "construction": true});
            skLineSegment(sketch, "E95.MirrorCS", {"start": v(-3.9, -7.65) * mm, "end": v(-4.15, -7.65) * mm});
            skLineSegment(sketch, "E96.MirrorCS", {"start": v(-26.76, -7.65) * mm, "end": v(-27.01, -7.65) * mm});
            skLineSegment(sketch, "E97.MirrorCS", {"start": v(-42, 7.59) * mm, "end": v(-42.25, 7.59) * mm});
            skLineSegment(sketch, "E98.MirrorCS", {"start": v(-11.52, 7.59) * mm, "end": v(-11.77, 7.59) * mm});
            skLineSegment(sketch, "E99.MirrorCS", {"start": v(-34.38, -7.65) * mm, "end": v(-34.63, -7.65) * mm});
            skLineSegment(sketch, "E100.MirrorCS", {"start": v(-49.62, -7.65) * mm, "end": v(-49.87, -7.65) * mm});
            skLineSegment(sketch, "E101.MirrorCS", {"start": v(-19.14, -7.65) * mm, "end": v(-19.4, -7.65) * mm});
            skLineSegment(sketch, "E102.MirrorCS", {"start": v(-3.9, 7.59) * mm, "end": v(-4.15, 7.59) * mm});
            skLineSegment(sketch, "E103.MirrorCS", {"start": v(-19.14, 7.59) * mm, "end": v(-19.4, 7.59) * mm});
            skLineSegment(sketch, "E104.MirrorCS", {"start": v(-42, -7.65) * mm, "end": v(-42.25, -7.65) * mm});
            skLineSegment(sketch, "E105.MirrorCS", {"start": v(-11.52, -7.65) * mm, "end": v(-11.77, -7.65) * mm});
            skLineSegment(sketch, "E106.MirrorCS", {"start": v(-34.38, 7.59) * mm, "end": v(-34.63, 7.59) * mm});
            skLineSegment(sketch, "E107.MirrorCS", {"start": v(-49.62, 7.59) * mm, "end": v(-49.87, 7.59) * mm});
            skLineSegment(sketch, "E108.MirrorCS", {"start": v(-26.76, 7.59) * mm, "end": v(-27.01, 7.59) * mm});
            skLineSegment(sketch, "E109.MirrorCS", {"start": v(-16.6, -7.65) * mm, "end": v(-16.85, -7.65) * mm});
            skLineSegment(sketch, "E110.MirrorCS", {"start": v(-36.92, -7.65) * mm, "end": v(-37.17, -7.65) * mm});
            skLineSegment(sketch, "E111.MirrorCS", {"start": v(-47.08, -7.65) * mm, "end": v(-47.33, -7.65) * mm});
            skLineSegment(sketch, "E112.MirrorCS", {"start": v(-6.44, -7.65) * mm, "end": v(-6.7, -7.65) * mm});
            skLineSegment(sketch, "E113.MirrorCS", {"start": v(-52.16, 7.59) * mm, "end": v(-52.41, 7.59) * mm});
            skLineSegment(sketch, "E114.MirrorCS", {"start": v(-21.68, 7.59) * mm, "end": v(-21.93, 7.59) * mm});
            skLineSegment(sketch, "E115.MirrorCS", {"start": v(-31.84, 7.59) * mm, "end": v(-32.1, 7.59) * mm});
            skLineSegment(sketch, "E116.MirrorCS", {"start": v(-54.7, -7.65) * mm, "end": v(-54.95, -7.65) * mm});
            skLineSegment(sketch, "E117.MirrorCS", {"start": v(-14.06, -7.65) * mm, "end": v(-14.31, -7.65) * mm});
            skLineSegment(sketch, "E118.MirrorCS", {"start": v(-24.22, -7.65) * mm, "end": v(-24.47, -7.65) * mm});
            skLineSegment(sketch, "E119.MirrorCS", {"start": v(-44.54, -7.65) * mm, "end": v(-44.8, -7.65) * mm});
            skLineSegment(sketch, "E120.MirrorCS", {"start": v(-39.46, -7.65) * mm, "end": v(-39.71, -7.65) * mm});
            skLineSegment(sketch, "E121.MirrorCS", {"start": v(-8.98, -7.65) * mm, "end": v(-9.23, -7.65) * mm});
            skLineSegment(sketch, "E122.MirrorCS", {"start": v(-29.3, -7.65) * mm, "end": v(-29.55, -7.65) * mm});
            skLineSegment(sketch, "E123.MirrorCS", {"start": v(-6.44, 7.59) * mm, "end": v(-6.7, 7.59) * mm});
            skLineSegment(sketch, "E124.MirrorCS", {"start": v(-14.06, 7.59) * mm, "end": v(-14.31, 7.59) * mm});
            skLineSegment(sketch, "E125.MirrorCS", {"start": v(-52.16, -7.65) * mm, "end": v(-52.41, -7.65) * mm});
            skLineSegment(sketch, "E126.MirrorCS", {"start": v(-39.46, 7.59) * mm, "end": v(-39.71, 7.59) * mm});
            skLineSegment(sketch, "E127.MirrorCS", {"start": v(-54.7, 7.59) * mm, "end": v(-54.95, 7.59) * mm});
            skLineSegment(sketch, "E128.MirrorCS", {"start": v(-8.98, 7.59) * mm, "end": v(-9.23, 7.59) * mm});
            skLineSegment(sketch, "E129.MirrorCS", {"start": v(-21.68, -7.65) * mm, "end": v(-21.93, -7.65) * mm});
            skLineSegment(sketch, "E130.MirrorCS", {"start": v(-29.3, 7.59) * mm, "end": v(-29.55, 7.59) * mm});
            skLineSegment(sketch, "E131.MirrorCS", {"start": v(-24.22, 7.59) * mm, "end": v(-24.47, 7.59) * mm});
            skLineSegment(sketch, "E132.MirrorCS", {"start": v(-31.84, -7.65) * mm, "end": v(-32.1, -7.65) * mm});
            skLineSegment(sketch, "E133.MirrorCS", {"start": v(-16.6, 7.59) * mm, "end": v(-16.85, 7.59) * mm});
            skLineSegment(sketch, "E134.MirrorCS", {"start": v(-36.92, 7.59) * mm, "end": v(-37.17, 7.59) * mm});
            skLineSegment(sketch, "E135.MirrorCS", {"start": v(-44.54, 7.59) * mm, "end": v(-44.8, 7.59) * mm});
            skLineSegment(sketch, "E136.MirrorCS", {"start": v(-47.08, 7.59) * mm, "end": v(-47.33, 7.59) * mm});
            skLineSegment(sketch, "E137.MirrorCS", {"start": v(-19.14, -7.65) * mm, "end": v(-19.14, 7.59) * mm});
            skLineSegment(sketch, "E138.MirrorCS", {"start": v(-34.63, -7.65) * mm, "end": v(-34.63, 7.59) * mm});
            skLineSegment(sketch, "E139.MirrorCS", {"start": v(-49.62, -7.65) * mm, "end": v(-49.62, 7.59) * mm});
            skLineSegment(sketch, "E140.MirrorCS", {"start": v(-42, -7.65) * mm, "end": v(-42, 7.59) * mm});
            skLineSegment(sketch, "E141.MirrorCS", {"start": v(-4.15, -7.65) * mm, "end": v(-4.15, 7.59) * mm});
            skLineSegment(sketch, "E142.MirrorCS", {"start": v(-26.76, -7.65) * mm, "end": v(-26.76, 7.59) * mm});
            skLineSegment(sketch, "E143.MirrorCS", {"start": v(-11.52, -7.65) * mm, "end": v(-11.52, 7.59) * mm});
            skLineSegment(sketch, "E144.MirrorCS", {"start": v(-14.06, -7.65) * mm, "end": v(-14.06, 7.59) * mm});
            skLineSegment(sketch, "E145.MirrorCS", {"start": v(-24.22, -7.65) * mm, "end": v(-24.22, 7.59) * mm});
            skLineSegment(sketch, "E146.MirrorCS", {"start": v(-34.38, -7.65) * mm, "end": v(-34.38, 7.59) * mm});
            skLineSegment(sketch, "E147.MirrorCS", {"start": v(-44.54, -7.65) * mm, "end": v(-44.54, 7.59) * mm});
            skLineSegment(sketch, "E148.MirrorCS", {"start": v(-3.9, -7.65) * mm, "end": v(-3.9, 7.59) * mm});
            skLineSegment(sketch, "E149.MirrorCS", {"start": v(-16.85, -7.65) * mm, "end": v(-16.85, 7.59) * mm});
            skLineSegment(sketch, "E150.MirrorCS", {"start": v(-27.01, -7.65) * mm, "end": v(-27.01, 7.59) * mm});
            skLineSegment(sketch, "E151.MirrorCS", {"start": v(-37.17, -7.65) * mm, "end": v(-37.17, 7.59) * mm});
            skLineSegment(sketch, "E152.MirrorCS", {"start": v(-47.33, -7.65) * mm, "end": v(-47.33, 7.59) * mm});
            skLineSegment(sketch, "E153.MirrorCS", {"start": v(-54.7, -7.65) * mm, "end": v(-54.7, 7.59) * mm});
            skLineSegment(sketch, "E154.MirrorCS", {"start": v(-6.7, -7.65) * mm, "end": v(-6.7, 7.59) * mm});
            skLineSegment(sketch, "E155.MirrorCS", {"start": v(-39.71, -7.65) * mm, "end": v(-39.71, 7.59) * mm});
            skLineSegment(sketch, "E156.MirrorCS", {"start": v(-49.87, -7.65) * mm, "end": v(-49.87, 7.59) * mm});
            skLineSegment(sketch, "E157.MirrorCS", {"start": v(-9.23, -7.65) * mm, "end": v(-9.23, 7.59) * mm});
            skLineSegment(sketch, "E158.MirrorCS", {"start": v(-19.4, -7.65) * mm, "end": v(-19.4, 7.59) * mm});
            skLineSegment(sketch, "E159.MirrorCS", {"start": v(-29.55, -7.65) * mm, "end": v(-29.55, 7.59) * mm});
            skLineSegment(sketch, "E160.MirrorCS", {"start": v(-42.25, -7.65) * mm, "end": v(-42.25, 7.59) * mm});
            skLineSegment(sketch, "E161.MirrorCS", {"start": v(-52.41, -7.65) * mm, "end": v(-52.41, 7.59) * mm});
            skLineSegment(sketch, "E162.MirrorCS", {"start": v(-54.95, -7.65) * mm, "end": v(-54.95, 7.59) * mm});
            skLineSegment(sketch, "E163.MirrorCS", {"start": v(-14.31, -7.65) * mm, "end": v(-14.31, 7.59) * mm});
            skLineSegment(sketch, "E164.MirrorCS", {"start": v(-29.3, -7.65) * mm, "end": v(-29.3, 7.59) * mm});
            skLineSegment(sketch, "E165.MirrorCS", {"start": v(-24.47, -7.65) * mm, "end": v(-24.47, 7.59) * mm});
            skLineSegment(sketch, "E166.MirrorCS", {"start": v(-39.46, -7.65) * mm, "end": v(-39.46, 7.59) * mm});
            skLineSegment(sketch, "E167.MirrorCS", {"start": v(-44.8, -7.65) * mm, "end": v(-44.8, 7.59) * mm});
            skLineSegment(sketch, "E168.MirrorCS", {"start": v(-36.92, -7.65) * mm, "end": v(-36.92, 7.59) * mm});
            skLineSegment(sketch, "E169.MirrorCS", {"start": v(-47.08, -7.65) * mm, "end": v(-47.08, 7.59) * mm});
            skLineSegment(sketch, "E170.MirrorCS", {"start": v(-31.84, -7.65) * mm, "end": v(-31.84, 7.59) * mm});
            skLineSegment(sketch, "E171.MirrorCS", {"start": v(-21.68, -7.65) * mm, "end": v(-21.68, 7.59) * mm});
            skLineSegment(sketch, "E172.MirrorCS", {"start": v(-32.1, -7.65) * mm, "end": v(-32.1, 7.59) * mm});
            skLineSegment(sketch, "E173.MirrorCS", {"start": v(-11.77, -7.65) * mm, "end": v(-11.77, 7.59) * mm});
            skLineSegment(sketch, "E174.MirrorCS", {"start": v(-16.6, -7.65) * mm, "end": v(-16.6, 7.59) * mm});
            skLineSegment(sketch, "E175.MirrorCS", {"start": v(-52.16, -7.65) * mm, "end": v(-52.16, 7.59) * mm});
            skLineSegment(sketch, "E176.MirrorCS", {"start": v(-21.93, -7.65) * mm, "end": v(-21.93, 7.59) * mm});
            skLineSegment(sketch, "E177.MirrorCS", {"start": v(-8.98, -7.65) * mm, "end": v(-8.98, 7.59) * mm});
            skLineSegment(sketch, "E178.MirrorCS", {"start": v(-6.44, -7.65) * mm, "end": v(-6.44, 7.59) * mm});
            skSolve(sketch);
        }
        {
            var Q0;
            Q0 = qSketchRegion(id + "F10", true);
            var Q1;
            {var subQ0=sQuery(id+"F10.wireOp",EDGE,"E94.20.0.0");var subQ1=sQuery(id+"F10.wireOp",EDGE,"E80");var subQ2=makeQuery(id+"F10.imprint","INTERSECT",VERTEX,{"derivedFrom":[subQ1,subQ0]});Q1=makeQuery(id+"F10.imprint","IMPRINT",FACE,{"disambiguationData":[TD([[makeQuery(id+"F10.imprint","IMPRINT",EDGE,{"disambiguationData":[TD([[subQ2,-1.0]])],"derivedFrom":subQ1}),1.0]])]});}
            var Q2;
            {var subQ0=sQuery(id+"F10.wireOp",EDGE,"E94.19.0.0");var subQ1=sQuery(id+"F10.wireOp",EDGE,"E79");var subQ2=makeQuery(id+"F10.imprint","INTERSECT",VERTEX,{"derivedFrom":[subQ1,subQ0]});Q2=makeQuery(id+"F10.imprint","IMPRINT",FACE,{"disambiguationData":[TD([[makeQuery(id+"F10.imprint","IMPRINT",EDGE,{"disambiguationData":[TD([[subQ2,-1.0]])],"derivedFrom":subQ1}),-1.0]])]});}
            var Q3;
            {var subQ0=sQuery(id+"F10.wireOp",EDGE,"E94.19.0.0");var subQ1=sQuery(id+"F10.wireOp",EDGE,"E80");var subQ2=makeQuery(id+"F10.imprint","INTERSECT",VERTEX,{"derivedFrom":[subQ1,subQ0]});Q3=makeQuery(id+"F10.imprint","IMPRINT",FACE,{"disambiguationData":[TD([[makeQuery(id+"F10.imprint","IMPRINT",EDGE,{"disambiguationData":[TD([[subQ2,-1.0]])],"derivedFrom":subQ1}),1.0]])]});}
            var Q4;
            {var subQ0=sQuery(id+"F10.wireOp",EDGE,"E94.18.0.0");var subQ1=sQuery(id+"F10.wireOp",EDGE,"E79");var subQ2=makeQuery(id+"F10.imprint","INTERSECT",VERTEX,{"derivedFrom":[subQ1,subQ0]});Q4=makeQuery(id+"F10.imprint","IMPRINT",FACE,{"disambiguationData":[TD([[makeQuery(id+"F10.imprint","IMPRINT",EDGE,{"disambiguationData":[TD([[subQ2,-1.0]])],"derivedFrom":subQ1}),-1.0]])]});}
            var Q5;
            {var subQ0=sQuery(id+"F10.wireOp",EDGE,"E94.17.0.0");var subQ1=sQuery(id+"F10.wireOp",EDGE,"E79");var subQ2=makeQuery(id+"F10.imprint","INTERSECT",VERTEX,{"derivedFrom":[subQ1,subQ0]});Q5=makeQuery(id+"F10.imprint","IMPRINT",FACE,{"disambiguationData":[TD([[makeQuery(id+"F10.imprint","IMPRINT",EDGE,{"disambiguationData":[TD([[subQ2,-1.0]])],"derivedFrom":subQ1}),-1.0]])]});}
            var Q6;
            {var subQ0=sQuery(id+"F10.wireOp",EDGE,"E94.16.0.0");var subQ1=sQuery(id+"F10.wireOp",EDGE,"E79");var subQ2=makeQuery(id+"F10.imprint","INTERSECT",VERTEX,{"derivedFrom":[subQ1,subQ0]});Q6=makeQuery(id+"F10.imprint","IMPRINT",FACE,{"disambiguationData":[TD([[makeQuery(id+"F10.imprint","IMPRINT",EDGE,{"disambiguationData":[TD([[subQ2,-1.0]])],"derivedFrom":subQ1}),-1.0]])]});}
            var Q7;
            {var subQ0=sQuery(id+"F10.wireOp",EDGE,"E94.15.0.0");var subQ1=sQuery(id+"F10.wireOp",EDGE,"E79");var subQ2=makeQuery(id+"F10.imprint","INTERSECT",VERTEX,{"derivedFrom":[subQ1,subQ0]});Q7=makeQuery(id+"F10.imprint","IMPRINT",FACE,{"disambiguationData":[TD([[makeQuery(id+"F10.imprint","IMPRINT",EDGE,{"disambiguationData":[TD([[subQ2,-1.0]])],"derivedFrom":subQ1}),-1.0]])]});}
            var Q8;
            {var subQ0=sQuery(id+"F10.wireOp",EDGE,"E94.14.0.0");var subQ1=sQuery(id+"F10.wireOp",EDGE,"E79");var subQ2=makeQuery(id+"F10.imprint","INTERSECT",VERTEX,{"derivedFrom":[subQ1,subQ0]});Q8=makeQuery(id+"F10.imprint","IMPRINT",FACE,{"disambiguationData":[TD([[makeQuery(id+"F10.imprint","IMPRINT",EDGE,{"disambiguationData":[TD([[subQ2,-1.0]])],"derivedFrom":subQ1}),-1.0]])]});}
            var Q9;
            {var subQ0=sQuery(id+"F10.wireOp",EDGE,"E94.20.0.0");var subQ1=sQuery(id+"F10.wireOp",EDGE,"E79");var subQ2=makeQuery(id+"F10.imprint","INTERSECT",VERTEX,{"derivedFrom":[subQ1,subQ0]});Q9=makeQuery(id+"F10.imprint","IMPRINT",FACE,{"disambiguationData":[TD([[makeQuery(id+"F10.imprint","IMPRINT",EDGE,{"disambiguationData":[TD([[subQ2,-1.0]])],"derivedFrom":subQ1}),-1.0]])]});}
            var Q10;
            {var subQ0=sQuery(id+"F10.wireOp",EDGE,"E94.13.0.0");var subQ1=sQuery(id+"F10.wireOp",EDGE,"E79");var subQ2=makeQuery(id+"F10.imprint","INTERSECT",VERTEX,{"derivedFrom":[subQ1,subQ0]});Q10=makeQuery(id+"F10.imprint","IMPRINT",FACE,{"disambiguationData":[TD([[makeQuery(id+"F10.imprint","IMPRINT",EDGE,{"disambiguationData":[TD([[subQ2,-1.0]])],"derivedFrom":subQ1}),-1.0]])]});}
            var Q11;
            {var subQ0=sQuery(id+"F10.wireOp",EDGE,"E94.12.0.0");var subQ1=sQuery(id+"F10.wireOp",EDGE,"E79");var subQ2=makeQuery(id+"F10.imprint","INTERSECT",VERTEX,{"derivedFrom":[subQ1,subQ0]});Q11=makeQuery(id+"F10.imprint","IMPRINT",FACE,{"disambiguationData":[TD([[makeQuery(id+"F10.imprint","IMPRINT",EDGE,{"disambiguationData":[TD([[subQ2,-1.0]])],"derivedFrom":subQ1}),-1.0]])]});}
            var Q12;
            {var subQ0=sQuery(id+"F10.wireOp",EDGE,"E94.11.0.0");var subQ1=sQuery(id+"F10.wireOp",EDGE,"E79");var subQ2=makeQuery(id+"F10.imprint","INTERSECT",VERTEX,{"derivedFrom":[subQ1,subQ0]});Q12=makeQuery(id+"F10.imprint","IMPRINT",FACE,{"disambiguationData":[TD([[makeQuery(id+"F10.imprint","IMPRINT",EDGE,{"disambiguationData":[TD([[subQ2,-1.0]])],"derivedFrom":subQ1}),-1.0]])]});}
            var Q13;
            {var subQ0=sQuery(id+"F10.wireOp",EDGE,"E94.10.0.0");var subQ1=sQuery(id+"F10.wireOp",EDGE,"E79");var subQ2=makeQuery(id+"F10.imprint","INTERSECT",VERTEX,{"derivedFrom":[subQ1,subQ0]});Q13=makeQuery(id+"F10.imprint","IMPRINT",FACE,{"disambiguationData":[TD([[makeQuery(id+"F10.imprint","IMPRINT",EDGE,{"disambiguationData":[TD([[subQ2,-1.0]])],"derivedFrom":subQ1}),-1.0]])]});}
            var Q14;
            {var subQ0=sQuery(id+"F10.wireOp",EDGE,"E94.9.0.0");var subQ1=sQuery(id+"F10.wireOp",EDGE,"E80");var subQ2=makeQuery(id+"F10.imprint","INTERSECT",VERTEX,{"derivedFrom":[subQ1,subQ0]});Q14=makeQuery(id+"F10.imprint","IMPRINT",FACE,{"disambiguationData":[TD([[makeQuery(id+"F10.imprint","IMPRINT",EDGE,{"disambiguationData":[TD([[subQ2,-1.0]])],"derivedFrom":subQ1}),1.0]])]});}
            var Q15;
            {var subQ0=sQuery(id+"F10.wireOp",EDGE,"E94.10.0.0");var subQ1=sQuery(id+"F10.wireOp",EDGE,"E80");var subQ2=makeQuery(id+"F10.imprint","INTERSECT",VERTEX,{"derivedFrom":[subQ1,subQ0]});Q15=makeQuery(id+"F10.imprint","IMPRINT",FACE,{"disambiguationData":[TD([[makeQuery(id+"F10.imprint","IMPRINT",EDGE,{"disambiguationData":[TD([[subQ2,-1.0]])],"derivedFrom":subQ1}),1.0]])]});}
            var Q16;
            {var subQ0=sQuery(id+"F10.wireOp",EDGE,"E94.9.0.0");var subQ1=sQuery(id+"F10.wireOp",EDGE,"E79");var subQ2=makeQuery(id+"F10.imprint","INTERSECT",VERTEX,{"derivedFrom":[subQ1,subQ0]});Q16=makeQuery(id+"F10.imprint","IMPRINT",FACE,{"disambiguationData":[TD([[makeQuery(id+"F10.imprint","IMPRINT",EDGE,{"disambiguationData":[TD([[subQ2,-1.0]])],"derivedFrom":subQ1}),-1.0]])]});}
            var Q17;
            {var subQ0=sQuery(id+"F10.wireOp",EDGE,"E94.8.0.0");var subQ1=sQuery(id+"F10.wireOp",EDGE,"E79");var subQ2=makeQuery(id+"F10.imprint","INTERSECT",VERTEX,{"derivedFrom":[subQ1,subQ0]});Q17=makeQuery(id+"F10.imprint","IMPRINT",FACE,{"disambiguationData":[TD([[makeQuery(id+"F10.imprint","IMPRINT",EDGE,{"disambiguationData":[TD([[subQ2,-1.0]])],"derivedFrom":subQ1}),-1.0]])]});}
            var Q18;
            {var subQ0=sQuery(id+"F10.wireOp",EDGE,"E94.7.0.0");var subQ1=sQuery(id+"F10.wireOp",EDGE,"E79");var subQ2=makeQuery(id+"F10.imprint","INTERSECT",VERTEX,{"derivedFrom":[subQ1,subQ0]});Q18=makeQuery(id+"F10.imprint","IMPRINT",FACE,{"disambiguationData":[TD([[makeQuery(id+"F10.imprint","IMPRINT",EDGE,{"disambiguationData":[TD([[subQ2,-1.0]])],"derivedFrom":subQ1}),-1.0]])]});}
            var Q19;
            {var subQ0=sQuery(id+"F10.wireOp",EDGE,"E94.6.0.0");var subQ1=sQuery(id+"F10.wireOp",EDGE,"E79");var subQ2=makeQuery(id+"F10.imprint","INTERSECT",VERTEX,{"derivedFrom":[subQ1,subQ0]});Q19=makeQuery(id+"F10.imprint","IMPRINT",FACE,{"disambiguationData":[TD([[makeQuery(id+"F10.imprint","IMPRINT",EDGE,{"disambiguationData":[TD([[subQ2,-1.0]])],"derivedFrom":subQ1}),-1.0]])]});}
            var Q20;
            {var subQ0=sQuery(id+"F10.wireOp",EDGE,"E94.5.0.0");var subQ1=sQuery(id+"F10.wireOp",EDGE,"E79");var subQ2=makeQuery(id+"F10.imprint","INTERSECT",VERTEX,{"derivedFrom":[subQ1,subQ0]});Q20=makeQuery(id+"F10.imprint","IMPRINT",FACE,{"disambiguationData":[TD([[makeQuery(id+"F10.imprint","IMPRINT",EDGE,{"disambiguationData":[TD([[subQ2,-1.0]])],"derivedFrom":subQ1}),-1.0]])]});}
            var Q21;
            {var subQ0=sQuery(id+"F10.wireOp",EDGE,"E94.4.0.0");var subQ1=sQuery(id+"F10.wireOp",EDGE,"E79");var subQ2=makeQuery(id+"F10.imprint","INTERSECT",VERTEX,{"derivedFrom":[subQ1,subQ0]});Q21=makeQuery(id+"F10.imprint","IMPRINT",FACE,{"disambiguationData":[TD([[makeQuery(id+"F10.imprint","IMPRINT",EDGE,{"disambiguationData":[TD([[subQ2,-1.0]])],"derivedFrom":subQ1}),-1.0]])]});}
            var Q22;
            {var subQ0=sQuery(id+"F10.wireOp",EDGE,"E94.3.0.0");var subQ1=sQuery(id+"F10.wireOp",EDGE,"E79");var subQ2=makeQuery(id+"F10.imprint","INTERSECT",VERTEX,{"derivedFrom":[subQ1,subQ0]});Q22=makeQuery(id+"F10.imprint","IMPRINT",FACE,{"disambiguationData":[TD([[makeQuery(id+"F10.imprint","IMPRINT",EDGE,{"disambiguationData":[TD([[subQ2,-1.0]])],"derivedFrom":subQ1}),-1.0]])]});}
            var Q23;
            {var subQ0=sQuery(id+"F10.wireOp",EDGE,"E94.2.0.0");var subQ1=sQuery(id+"F10.wireOp",EDGE,"E79");var subQ2=makeQuery(id+"F10.imprint","INTERSECT",VERTEX,{"derivedFrom":[subQ1,subQ0]});Q23=makeQuery(id+"F10.imprint","IMPRINT",FACE,{"disambiguationData":[TD([[makeQuery(id+"F10.imprint","IMPRINT",EDGE,{"disambiguationData":[TD([[subQ2,-1.0]])],"derivedFrom":subQ1}),-1.0]])]});}
            var Q24;
            {var subQ0=sQuery(id+"F10.wireOp",EDGE,"E94.1.0.0");var subQ1=sQuery(id+"F10.wireOp",EDGE,"E79");var subQ2=makeQuery(id+"F10.imprint","INTERSECT",VERTEX,{"derivedFrom":[subQ1,subQ0]});Q24=makeQuery(id+"F10.imprint","IMPRINT",FACE,{"disambiguationData":[TD([[makeQuery(id+"F10.imprint","IMPRINT",EDGE,{"disambiguationData":[TD([[subQ2,-1.0]])],"derivedFrom":subQ1}),-1.0]])]});}
            var Q25;
            {var subQ0=sQuery(id+"F10.wireOp",EDGE,"E83.left");var subQ1=sQuery(id+"F10.wireOp",EDGE,"E79");var subQ2=makeQuery(id+"F10.imprint","INTERSECT",VERTEX,{"derivedFrom":[subQ1,subQ0]});Q25=makeQuery(id+"F10.imprint","IMPRINT",FACE,{"disambiguationData":[TD([[makeQuery(id+"F10.imprint","IMPRINT",EDGE,{"disambiguationData":[TD([[subQ2,-1.0]])],"derivedFrom":subQ1}),-1.0]])]});}
            var Q26;
            {var subQ0=sQuery(id+"F10.wireOp",EDGE,"E83.left");var subQ1=sQuery(id+"F10.wireOp",EDGE,"E80");var subQ2=makeQuery(id+"F10.imprint","INTERSECT",VERTEX,{"derivedFrom":[subQ1,subQ0]});Q26=makeQuery(id+"F10.imprint","IMPRINT",FACE,{"disambiguationData":[TD([[makeQuery(id+"F10.imprint","IMPRINT",EDGE,{"disambiguationData":[TD([[subQ2,-1.0]])],"derivedFrom":subQ1}),1.0]])]});}
            var Q27;
            {var subQ0=sQuery(id+"F10.wireOp",EDGE,"E92.MirrorCS");var subQ1=sQuery(id+"F10.wireOp",EDGE,"E89.MirrorCS");var subQ2=makeQuery(id+"F10.imprint","INTERSECT",VERTEX,{"derivedFrom":[subQ1,subQ0]});Q27=makeQuery(id+"F10.imprint","IMPRINT",FACE,{"disambiguationData":[TD([[makeQuery(id+"F10.imprint","IMPRINT",EDGE,{"disambiguationData":[TD([[subQ2,-1.0]])],"derivedFrom":subQ1}),1.0]])]});}
            var Q28;
            {var subQ0=sQuery(id+"F10.wireOp",EDGE,"E87.MirrorCS");var subQ1=sQuery(id+"F10.wireOp",EDGE,"E91.MirrorCS");var subQ2=makeQuery(id+"F10.imprint","INTERSECT",VERTEX,{"derivedFrom":[subQ1,subQ0]});Q28=makeQuery(id+"F10.imprint","IMPRINT",FACE,{"disambiguationData":[TD([[makeQuery(id+"F10.imprint","IMPRINT",EDGE,{"disambiguationData":[TD([[subQ2,-1.0]])],"derivedFrom":subQ1}),-1.0]])]});}
            var Q29;
            {var subQ0=sQuery(id+"F10.wireOp",EDGE,"E148.MirrorCS");var subQ1=sQuery(id+"F10.wireOp",EDGE,"E89.MirrorCS");var subQ2=makeQuery(id+"F10.imprint","INTERSECT",VERTEX,{"derivedFrom":[subQ1,subQ0]});Q29=makeQuery(id+"F10.imprint","IMPRINT",FACE,{"disambiguationData":[TD([[makeQuery(id+"F10.imprint","IMPRINT",EDGE,{"disambiguationData":[TD([[subQ2,-1.0]])],"derivedFrom":subQ1}),1.0]])]});}
            var Q30;
            {var subQ0=sQuery(id+"F10.wireOp",EDGE,"E178.MirrorCS");var subQ1=sQuery(id+"F10.wireOp",EDGE,"E89.MirrorCS");var subQ2=makeQuery(id+"F10.imprint","INTERSECT",VERTEX,{"derivedFrom":[subQ1,subQ0]});Q30=makeQuery(id+"F10.imprint","IMPRINT",FACE,{"disambiguationData":[TD([[makeQuery(id+"F10.imprint","IMPRINT",EDGE,{"disambiguationData":[TD([[subQ2,-1.0]])],"derivedFrom":subQ1}),1.0]])]});}
            var Q31;
            {var subQ0=sQuery(id+"F10.wireOp",EDGE,"E177.MirrorCS");var subQ1=sQuery(id+"F10.wireOp",EDGE,"E89.MirrorCS");var subQ2=makeQuery(id+"F10.imprint","INTERSECT",VERTEX,{"derivedFrom":[subQ1,subQ0]});Q31=makeQuery(id+"F10.imprint","IMPRINT",FACE,{"disambiguationData":[TD([[makeQuery(id+"F10.imprint","IMPRINT",EDGE,{"disambiguationData":[TD([[subQ2,-1.0]])],"derivedFrom":subQ1}),1.0]])]});}
            var Q32;
            {var subQ0=sQuery(id+"F10.wireOp",EDGE,"E143.MirrorCS");var subQ1=sQuery(id+"F10.wireOp",EDGE,"E89.MirrorCS");var subQ2=makeQuery(id+"F10.imprint","INTERSECT",VERTEX,{"derivedFrom":[subQ1,subQ0]});Q32=makeQuery(id+"F10.imprint","IMPRINT",FACE,{"disambiguationData":[TD([[makeQuery(id+"F10.imprint","IMPRINT",EDGE,{"disambiguationData":[TD([[subQ2,-1.0]])],"derivedFrom":subQ1}),1.0]])]});}
            var Q33;
            {var subQ0=sQuery(id+"F10.wireOp",EDGE,"E144.MirrorCS");var subQ1=sQuery(id+"F10.wireOp",EDGE,"E89.MirrorCS");var subQ2=makeQuery(id+"F10.imprint","INTERSECT",VERTEX,{"derivedFrom":[subQ1,subQ0]});Q33=makeQuery(id+"F10.imprint","IMPRINT",FACE,{"disambiguationData":[TD([[makeQuery(id+"F10.imprint","IMPRINT",EDGE,{"disambiguationData":[TD([[subQ2,-1.0]])],"derivedFrom":subQ1}),1.0]])]});}
            var Q34;
            {var subQ0=sQuery(id+"F10.wireOp",EDGE,"E174.MirrorCS");var subQ1=sQuery(id+"F10.wireOp",EDGE,"E89.MirrorCS");var subQ2=makeQuery(id+"F10.imprint","INTERSECT",VERTEX,{"derivedFrom":[subQ1,subQ0]});Q34=makeQuery(id+"F10.imprint","IMPRINT",FACE,{"disambiguationData":[TD([[makeQuery(id+"F10.imprint","IMPRINT",EDGE,{"disambiguationData":[TD([[subQ2,-1.0]])],"derivedFrom":subQ1}),1.0]])]});}
            var Q35;
            {var subQ0=sQuery(id+"F10.wireOp",EDGE,"E137.MirrorCS");var subQ1=sQuery(id+"F10.wireOp",EDGE,"E89.MirrorCS");var subQ2=makeQuery(id+"F10.imprint","INTERSECT",VERTEX,{"derivedFrom":[subQ1,subQ0]});Q35=makeQuery(id+"F10.imprint","IMPRINT",FACE,{"disambiguationData":[TD([[makeQuery(id+"F10.imprint","IMPRINT",EDGE,{"disambiguationData":[TD([[subQ2,-1.0]])],"derivedFrom":subQ1}),1.0]])]});}
            var Q36;
            {var subQ0=sQuery(id+"F10.wireOp",EDGE,"E171.MirrorCS");var subQ1=sQuery(id+"F10.wireOp",EDGE,"E89.MirrorCS");var subQ2=makeQuery(id+"F10.imprint","INTERSECT",VERTEX,{"derivedFrom":[subQ1,subQ0]});Q36=makeQuery(id+"F10.imprint","IMPRINT",FACE,{"disambiguationData":[TD([[makeQuery(id+"F10.imprint","IMPRINT",EDGE,{"disambiguationData":[TD([[subQ2,-1.0]])],"derivedFrom":subQ1}),1.0]])]});}
            var Q37;
            {var subQ0=sQuery(id+"F10.wireOp",EDGE,"E145.MirrorCS");var subQ1=sQuery(id+"F10.wireOp",EDGE,"E87.MirrorCS");var subQ2=makeQuery(id+"F10.imprint","INTERSECT",VERTEX,{"derivedFrom":[subQ1,subQ0]});Q37=makeQuery(id+"F10.imprint","IMPRINT",FACE,{"disambiguationData":[TD([[makeQuery(id+"F10.imprint","IMPRINT",EDGE,{"disambiguationData":[TD([[subQ2,-1.0]])],"derivedFrom":subQ1}),-1.0]])]});}
            var Q38;
            {var subQ0=sQuery(id+"F10.wireOp",EDGE,"E145.MirrorCS");var subQ1=sQuery(id+"F10.wireOp",EDGE,"E89.MirrorCS");var subQ2=makeQuery(id+"F10.imprint","INTERSECT",VERTEX,{"derivedFrom":[subQ1,subQ0]});Q38=makeQuery(id+"F10.imprint","IMPRINT",FACE,{"disambiguationData":[TD([[makeQuery(id+"F10.imprint","IMPRINT",EDGE,{"disambiguationData":[TD([[subQ2,-1.0]])],"derivedFrom":subQ1}),1.0]])]});}
            var Q39;
            {var subQ0=sQuery(id+"F10.wireOp",EDGE,"E142.MirrorCS");var subQ1=sQuery(id+"F10.wireOp",EDGE,"E89.MirrorCS");var subQ2=makeQuery(id+"F10.imprint","INTERSECT",VERTEX,{"derivedFrom":[subQ1,subQ0]});Q39=makeQuery(id+"F10.imprint","IMPRINT",FACE,{"disambiguationData":[TD([[makeQuery(id+"F10.imprint","IMPRINT",EDGE,{"disambiguationData":[TD([[subQ2,-1.0]])],"derivedFrom":subQ1}),1.0]])]});}
            var Q40;
            {var subQ0=sQuery(id+"F10.wireOp",EDGE,"E142.MirrorCS");var subQ1=sQuery(id+"F10.wireOp",EDGE,"E87.MirrorCS");var subQ2=makeQuery(id+"F10.imprint","INTERSECT",VERTEX,{"derivedFrom":[subQ1,subQ0]});Q40=makeQuery(id+"F10.imprint","IMPRINT",FACE,{"disambiguationData":[TD([[makeQuery(id+"F10.imprint","IMPRINT",EDGE,{"disambiguationData":[TD([[subQ2,-1.0]])],"derivedFrom":subQ1}),-1.0]])]});}
            var Q41;
            {var subQ0=sQuery(id+"F10.wireOp",EDGE,"E164.MirrorCS");var subQ1=sQuery(id+"F10.wireOp",EDGE,"E89.MirrorCS");var subQ2=makeQuery(id+"F10.imprint","INTERSECT",VERTEX,{"derivedFrom":[subQ1,subQ0]});Q41=makeQuery(id+"F10.imprint","IMPRINT",FACE,{"disambiguationData":[TD([[makeQuery(id+"F10.imprint","IMPRINT",EDGE,{"disambiguationData":[TD([[subQ2,-1.0]])],"derivedFrom":subQ1}),1.0]])]});}
            var Q42;
            {var subQ0=sQuery(id+"F10.wireOp",EDGE,"E170.MirrorCS");var subQ1=sQuery(id+"F10.wireOp",EDGE,"E89.MirrorCS");var subQ2=makeQuery(id+"F10.imprint","INTERSECT",VERTEX,{"derivedFrom":[subQ1,subQ0]});Q42=makeQuery(id+"F10.imprint","IMPRINT",FACE,{"disambiguationData":[TD([[makeQuery(id+"F10.imprint","IMPRINT",EDGE,{"disambiguationData":[TD([[subQ2,-1.0]])],"derivedFrom":subQ1}),1.0]])]});}
            var Q43;
            {var subQ0=sQuery(id+"F10.wireOp",EDGE,"E146.MirrorCS");var subQ1=sQuery(id+"F10.wireOp",EDGE,"E89.MirrorCS");var subQ2=makeQuery(id+"F10.imprint","INTERSECT",VERTEX,{"derivedFrom":[subQ1,subQ0]});Q43=makeQuery(id+"F10.imprint","IMPRINT",FACE,{"disambiguationData":[TD([[makeQuery(id+"F10.imprint","IMPRINT",EDGE,{"disambiguationData":[TD([[subQ2,-1.0]])],"derivedFrom":subQ1}),1.0]])]});}
            var Q44;
            {var subQ0=sQuery(id+"F10.wireOp",EDGE,"E168.MirrorCS");var subQ1=sQuery(id+"F10.wireOp",EDGE,"E89.MirrorCS");var subQ2=makeQuery(id+"F10.imprint","INTERSECT",VERTEX,{"derivedFrom":[subQ1,subQ0]});Q44=makeQuery(id+"F10.imprint","IMPRINT",FACE,{"disambiguationData":[TD([[makeQuery(id+"F10.imprint","IMPRINT",EDGE,{"disambiguationData":[TD([[subQ2,-1.0]])],"derivedFrom":subQ1}),1.0]])]});}
            var Q45;
            {var subQ0=sQuery(id+"F10.wireOp",EDGE,"E166.MirrorCS");var subQ1=sQuery(id+"F10.wireOp",EDGE,"E89.MirrorCS");var subQ2=makeQuery(id+"F10.imprint","INTERSECT",VERTEX,{"derivedFrom":[subQ1,subQ0]});Q45=makeQuery(id+"F10.imprint","IMPRINT",FACE,{"disambiguationData":[TD([[makeQuery(id+"F10.imprint","IMPRINT",EDGE,{"disambiguationData":[TD([[subQ2,-1.0]])],"derivedFrom":subQ1}),1.0]])]});}
            var Q46;
            {var subQ0=sQuery(id+"F10.wireOp",EDGE,"E140.MirrorCS");var subQ1=sQuery(id+"F10.wireOp",EDGE,"E89.MirrorCS");var subQ2=makeQuery(id+"F10.imprint","INTERSECT",VERTEX,{"derivedFrom":[subQ1,subQ0]});Q46=makeQuery(id+"F10.imprint","IMPRINT",FACE,{"disambiguationData":[TD([[makeQuery(id+"F10.imprint","IMPRINT",EDGE,{"disambiguationData":[TD([[subQ2,-1.0]])],"derivedFrom":subQ1}),1.0]])]});}
            var Q47;
            {var subQ0=sQuery(id+"F10.wireOp",EDGE,"E147.MirrorCS");var subQ1=sQuery(id+"F10.wireOp",EDGE,"E89.MirrorCS");var subQ2=makeQuery(id+"F10.imprint","INTERSECT",VERTEX,{"derivedFrom":[subQ1,subQ0]});Q47=makeQuery(id+"F10.imprint","IMPRINT",FACE,{"disambiguationData":[TD([[makeQuery(id+"F10.imprint","IMPRINT",EDGE,{"disambiguationData":[TD([[subQ2,-1.0]])],"derivedFrom":subQ1}),1.0]])]});}
            var Q48;
            {var subQ0=sQuery(id+"F10.wireOp",EDGE,"E169.MirrorCS");var subQ1=sQuery(id+"F10.wireOp",EDGE,"E89.MirrorCS");var subQ2=makeQuery(id+"F10.imprint","INTERSECT",VERTEX,{"derivedFrom":[subQ1,subQ0]});Q48=makeQuery(id+"F10.imprint","IMPRINT",FACE,{"disambiguationData":[TD([[makeQuery(id+"F10.imprint","IMPRINT",EDGE,{"disambiguationData":[TD([[subQ2,-1.0]])],"derivedFrom":subQ1}),1.0]])]});}
            var Q49;
            {var subQ0=sQuery(id+"F10.wireOp",EDGE,"E139.MirrorCS");var subQ1=sQuery(id+"F10.wireOp",EDGE,"E87.MirrorCS");var subQ2=makeQuery(id+"F10.imprint","INTERSECT",VERTEX,{"derivedFrom":[subQ1,subQ0]});Q49=makeQuery(id+"F10.imprint","IMPRINT",FACE,{"disambiguationData":[TD([[makeQuery(id+"F10.imprint","IMPRINT",EDGE,{"disambiguationData":[TD([[subQ2,-1.0]])],"derivedFrom":subQ1}),-1.0]])]});}
            var Q50;
            {var subQ0=sQuery(id+"F10.wireOp",EDGE,"E139.MirrorCS");var subQ1=sQuery(id+"F10.wireOp",EDGE,"E89.MirrorCS");var subQ2=makeQuery(id+"F10.imprint","INTERSECT",VERTEX,{"derivedFrom":[subQ1,subQ0]});Q50=makeQuery(id+"F10.imprint","IMPRINT",FACE,{"disambiguationData":[TD([[makeQuery(id+"F10.imprint","IMPRINT",EDGE,{"disambiguationData":[TD([[subQ2,-1.0]])],"derivedFrom":subQ1}),1.0]])]});}
            var Q51;
            {var subQ0=sQuery(id+"F10.wireOp",EDGE,"E175.MirrorCS");var subQ1=sQuery(id+"F10.wireOp",EDGE,"E89.MirrorCS");var subQ2=makeQuery(id+"F10.imprint","INTERSECT",VERTEX,{"derivedFrom":[subQ1,subQ0]});Q51=makeQuery(id+"F10.imprint","IMPRINT",FACE,{"disambiguationData":[TD([[makeQuery(id+"F10.imprint","IMPRINT",EDGE,{"disambiguationData":[TD([[subQ2,-1.0]])],"derivedFrom":subQ1}),1.0]])]});}
            var Q52;
            {var subQ0=sQuery(id+"F10.wireOp",EDGE,"E175.MirrorCS");var subQ1=sQuery(id+"F10.wireOp",EDGE,"E87.MirrorCS");var subQ2=makeQuery(id+"F10.imprint","INTERSECT",VERTEX,{"derivedFrom":[subQ1,subQ0]});Q52=makeQuery(id+"F10.imprint","IMPRINT",FACE,{"disambiguationData":[TD([[makeQuery(id+"F10.imprint","IMPRINT",EDGE,{"disambiguationData":[TD([[subQ2,-1.0]])],"derivedFrom":subQ1}),-1.0]])]});}
            extrude(context, id + "F11", {"entities" : qUnion([Q0, Q1, Q2, Q3, Q4, Q5, Q6, Q7, Q8, Q9, Q10, Q11, Q12, Q13, Q14, Q15, Q16, Q17, Q18, Q19, Q20, Q21, Q22, Q23, Q24, Q25, Q26, Q27, Q28, Q29, Q30, Q31, Q32, Q33, Q34, Q35, Q36, Q37, Q38, Q39, Q40, Q41, Q42, Q43, Q44, Q45, Q46, Q47, Q48, Q49, Q50, Q51, Q52]), "operationType" : NewBodyOperationType.REMOVE, "oppositeDirection" : true, "depth" : 0.25 * mm, "offsetDistance" : 25.4 * mm});
        }
        {
            var Q0;
            Q0=qCreatedBy(makeId("Top.planeOp"),FACE);
            var sketch = newSketch(context, id + "F12", { "sketchPlane" : qUnion([Q0])});
            skLineSegment(sketch, "E179", {"start": v(0, 10.58) * mm, "end": v(0, 12.72) * mm, "construction": true});
            skEllipticalArc(sketch, "E180", {});
            skEllipticalArc(sketch, "E181.MirrorC", {});
            const initialGuessF12  = {"E180": [0.003787650726735592, 0.00629799859598279, -1, 0, 0.00508, 0.00254, 0.7293607645811823, 5.553824542598404], "E181.MirrorC": [-0.003787650726735592, 0.00629799859598279, 1, 0, 0.00508, 0.00254, 0.7293607645811819, 5.553824542598404]};
            skSetInitialGuess(sketch, initialGuessF12);
            skSolve(sketch);
        }
        {
            var Q0;
            Q0=makeQuery(id+"F12.imprint","IMPRINT",FACE,{"disambiguationData":[TD([[makeQuery(id+"F12.imprint","IMPRINT",EDGE,{"derivedFrom":sQuery(id+"F12.wireOp",EDGE,"E180")}),1.0]])]});
            extrude(context, id + "F13", {"entities" : qUnion([Q0]), "operationType" : NewBodyOperationType.ADD, "depth" : 1.78 * mm, "offsetDistance" : 25.4 * mm});
        }
        {
            var Q0;
            Q0=makeQuery(id+"F13.opExtrude","CAP_FACE",FACE,{"disambiguationData":[OSD([sQuery(id+"F12.wireOp",EDGE,"E180"),sQuery(id+"F12.wireOp",EDGE,"E181.MirrorC")])],"isStart":false});
            var sketch = newSketch(context, id + "F14", { "sketchPlane" : qUnion([Q0])});
            skEllipse(sketch, "E182", {"center": v(-5.71, 6.47) * mm, "majorRadius": 2.25 * mm, "minorRadius": 1.5 * mm, "majorAxis": v(1, 0)});
            skEllipse(sketch, "E183", {"center": v(3.08, 6.37) * mm, "majorRadius": 3.22 * mm, "minorRadius": 1.5 * mm, "majorAxis": v(-1, 0)});
            skSolve(sketch);
        }
        {
            var Q0;
            Q0=makeQuery(id+"F14.imprint","IMPRINT",FACE,{"disambiguationData":[TD([[makeQuery(id+"F14.imprint","IMPRINT",EDGE,{"derivedFrom":sQuery(id+"F14.wireOp",EDGE,"E182")}),1.0]])]});
            var Q1;
            Q1=makeQuery(id+"F14.imprint","IMPRINT",FACE,{"disambiguationData":[TD([[makeQuery(id+"F14.imprint","IMPRINT",EDGE,{"derivedFrom":sQuery(id+"F14.wireOp",EDGE,"E183")}),1.0]])]});
            extrude(context, id + "F15", {"entities" : qUnion([Q0, Q1]), "operationType" : NewBodyOperationType.ADD, "depth" : 1.02 * mm, "offsetDistance" : 25.4 * mm});
        }
        {
            var Q0;
            Q0=makeQuery(id+"F15.opExtrude","CAP_FACE",FACE,{"disambiguationData":[OSD([sQuery(id+"F14.wireOp",EDGE,"E183")])],"isStart":false});
            var sketch = newSketch(context, id + "F16", { "sketchPlane" : qUnion([Q0])});
            skEllipse(sketch, "E184", {"center": v(2.62, 6.37) * mm, "majorRadius": 1.53 * mm, "minorRadius": 1.2 * mm, "majorAxis": v(1, 0)});
            skPoint(sketch, "E184.centerSnap0", {"position": v(-0.14, 6.37) * mm});
            skSolve(sketch);
        }
        {
            var Q0;
            Q0=makeQuery(id+"F16.imprint","IMPRINT",FACE,{"disambiguationData":[TD([[makeQuery(id+"F16.imprint","IMPRINT",EDGE,{"derivedFrom":sQuery(id+"F16.wireOp",EDGE,"E184")}),1.0]])]});
            extrude(context, id + "F17", {"entities" : qUnion([Q0]), "operationType" : NewBodyOperationType.ADD, "depth" : 0.76 * mm, "offsetDistance" : 25.4 * mm});
        }
        {
            var Q0;
            Q0=makeQuery(id+"F13.opExtrude","CAP_EDGE",EDGE,{"disambiguationData":[OSD([sQuery(id+"F12.wireOp",EDGE,"E181.MirrorC")])],"isStart":false});
            fillet(context, id + "F18", {"entities" : qUnion([Q0]), "radius" : 0.5 * mm, "tangentPropagation" : true, "allowEdgeOverflow" : false});
        }
        {
            var Q0;
            Q0=makeQuery(id+"F13.opExtrude","CAP_EDGE",EDGE,{"disambiguationData":[OSD([sQuery(id+"F12.wireOp",EDGE,"E180")])],"isStart":false});
            var Q1;
            Q1=makeQuery(id+"F15.opExtrude","CAP_EDGE",EDGE,{"disambiguationData":[OSD([sQuery(id+"F14.wireOp",EDGE,"E183")])],"isStart":false});
            var Q2;
            Q2=makeQuery(id+"F17.opExtrude","CAP_EDGE",EDGE,{"disambiguationData":[OSD([sQuery(id+"F16.wireOp",EDGE,"E184")])],"isStart":false});
            var Q3;
            Q3=makeQuery(id+"F15.opExtrude","CAP_EDGE",EDGE,{"disambiguationData":[OSD([sQuery(id+"F14.wireOp",EDGE,"E182")])],"isStart":false});
            fillet(context, id + "F19", {"entities" : qUnion([Q0, Q1, Q2, Q3]), "radius" : 0.13 * mm, "tangentPropagation" : true, "allowEdgeOverflow" : false});
        }
    });
